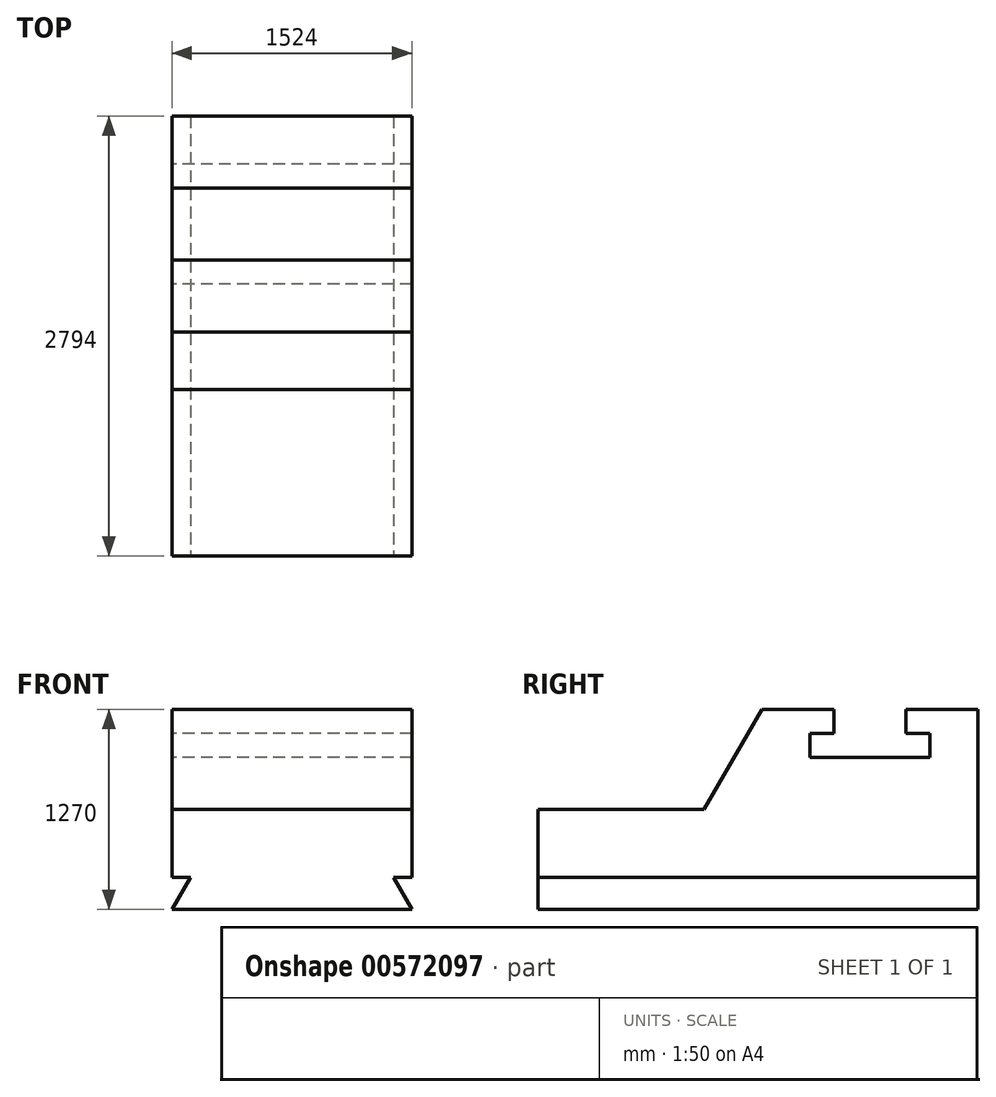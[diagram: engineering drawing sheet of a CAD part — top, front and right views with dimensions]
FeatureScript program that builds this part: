
annotation { "Feature Type Name" : "Feature", "Feature Type Description" : "" }
export const myFeature = defineFeature(function(context is Context, id is Id, definition is map)
    precondition{}
    {
        {
            var Q0;
            Q0=qCreatedBy(makeId("Right.planeOp"),FACE);
            var sketch = newSketch(context, id + "F0", { "sketchPlane" : qUnion([Q0])});
            skLineSegment(sketch, "E0", {"start": v(0, 0) * mm, "end": v(2794, 0) * mm});
            skLineSegment(sketch, "E1", {"start": v(2794, 0) * mm, "end": v(2794, 203.2) * mm});
            skLineSegment(sketch, "E2", {"start": v(2794, 203.2) * mm, "end": v(2794, 1270) * mm});
            skLineSegment(sketch, "E3", {"start": v(2794, 1270) * mm, "end": v(2336.8, 1270) * mm});
            skLineSegment(sketch, "E4", {"start": v(2336.8, 1270) * mm, "end": v(2336.8, 1117.6) * mm});
            skLineSegment(sketch, "E5", {"start": v(2336.8, 1117.6) * mm, "end": v(2489.2, 1117.6) * mm});
            skLineSegment(sketch, "E6", {"start": v(2489.2, 1117.6) * mm, "end": v(2489.2, 965.2) * mm});
            skLineSegment(sketch, "E7", {"start": v(2489.2, 965.2) * mm, "end": v(1727.2, 965.2) * mm});
            skLineSegment(sketch, "E8", {"start": v(1727.2, 965.2) * mm, "end": v(1727.2, 1117.6) * mm});
            skLineSegment(sketch, "E9", {"start": v(0, 214.14) * mm, "end": v(0, 0) * mm});
            skLineSegment(sketch, "E10", {"start": v(1727.2, 1117.6) * mm, "end": v(1879.6, 1117.6) * mm});
            skLineSegment(sketch, "E11", {"start": v(1879.6, 1117.6) * mm, "end": v(1879.6, 1270) * mm});
            skLineSegment(sketch, "E12", {"start": v(1879.6, 1270) * mm, "end": v(1422.4, 1270) * mm});
            skLineSegment(sketch, "E13", {"start": v(1422.4, 1270) * mm, "end": v(1055.78, 635) * mm});
            skLineSegment(sketch, "E14", {"start": v(1055.78, 635) * mm, "end": v(0, 635) * mm});
            skLineSegment(sketch, "E15", {"start": v(0, 635) * mm, "end": v(0, 0) * mm});
            skSolve(sketch);
        }
        {
            var Q0;
            Q0 = qSketchRegion(id + "F0", true);
            extrude(context, id + "F1", {"entities" : qUnion([Q0]), "depth" : 1524 * mm, "offsetDistance" : 25.4 * mm});
        }
        {
            var Q0;
            Q0=makeQuery(id+"F1.opExtrude","SWEPT_FACE",FACE,{"disambiguationData":[OSD([sQuery(id+"F0.wireOp",EDGE,"E15")])]});
            var sketch = newSketch(context, id + "F2", { "sketchPlane" : qUnion([Q0])});
            skLineSegment(sketch, "E16", {"start": v(1524, 0) * mm, "end": v(1524, 203.2) * mm});
            skLineSegment(sketch, "E17", {"start": v(1524, 203.2) * mm, "end": v(1406.68, 203.2) * mm});
            skLineSegment(sketch, "E18", {"start": v(1406.68, 203.2) * mm, "end": v(1524, 0) * mm});
            skLineSegment(sketch, "E19.MirrorCS", {"start": v(117.32, 203.2) * mm, "end": v(0, 0) * mm});
            skLineSegment(sketch, "E20.MirrorCS", {"start": v(0, 0) * mm, "end": v(0, 203.2) * mm});
            skLineSegment(sketch, "E21.MirrorCS", {"start": v(0, 203.2) * mm, "end": v(117.32, 203.2) * mm});
            skSolve(sketch);
        }
        {
            var Q0;
            Q0=makeQuery(id+"F2.imprint","IMPRINT",FACE,{"disambiguationData":[TD([[makeQuery(id+"F2.imprint","IMPRINT",EDGE,{"derivedFrom":sQuery(id+"F2.wireOp",EDGE,"E16")}),-1.0]])]});
            extrude(context, id + "F3", {"entities" : qUnion([Q0]), "operationType" : NewBodyOperationType.REMOVE, "endBound" : BoundingType.THROUGH_ALL, "oppositeDirection" : true, "depth" : 25.4 * mm, "offsetDistance" : 25.4 * mm});
        }
        {
            var Q0;
            Q0 = qSketchRegion(id + "F2", true);
            extrude(context, id + "F4", {"entities" : qUnion([Q0]), "operationType" : NewBodyOperationType.REMOVE, "endBound" : BoundingType.THROUGH_ALL, "oppositeDirection" : true, "depth" : 25.4 * mm, "offsetDistance" : 25.4 * mm});
        }
    });
